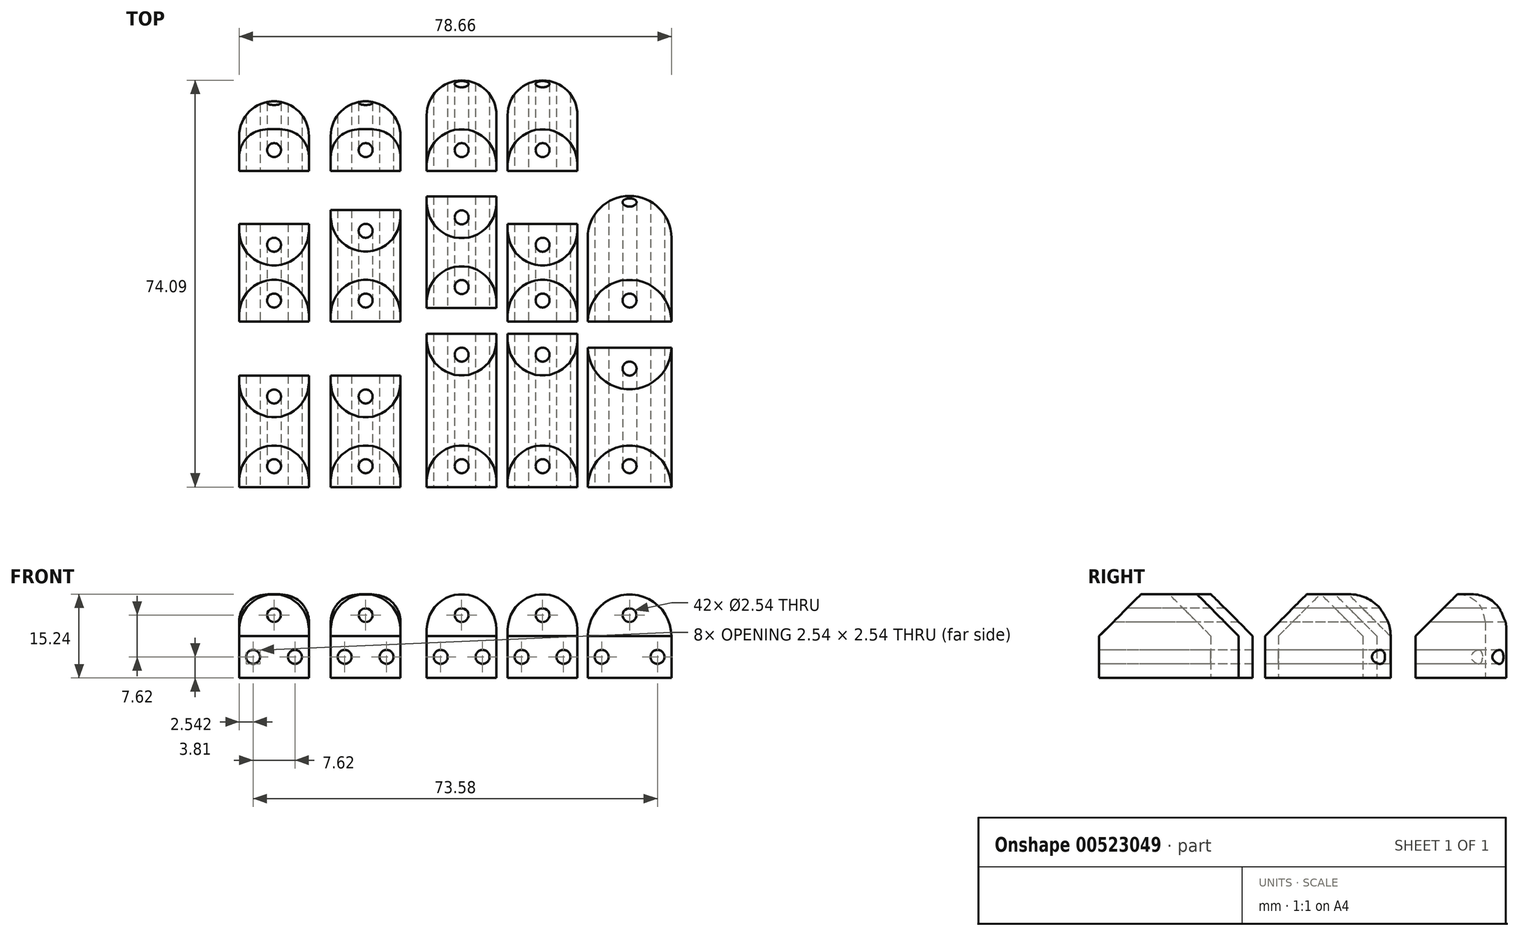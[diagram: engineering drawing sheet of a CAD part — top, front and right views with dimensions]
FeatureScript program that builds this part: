
annotation { "Feature Type Name" : "Feature", "Feature Type Description" : "" }
export const myFeature = defineFeature(function(context is Context, id is Id, definition is map)
    precondition{}
    {
        {
            var Q0;
            Q0=qCreatedBy(makeId("Top.planeOp"),FACE);
            var sketch = newSketch(context, id + "F0", { "sketchPlane" : qUnion([Q0])});
            skLineSegment(sketch, "E0.bottom", {"start": v(-28.43, 45.4) * mm, "end": v(-15.73, 45.4) * mm});
            skLineSegment(sketch, "E0.top", {"start": v(-28.43, 32.7) * mm, "end": v(-15.73, 32.7) * mm});
            skLineSegment(sketch, "E0.left", {"start": v(-28.43, 45.4) * mm, "end": v(-28.43, 32.7) * mm});
            skLineSegment(sketch, "E0.right", {"start": v(-15.73, 45.4) * mm, "end": v(-15.73, 32.7) * mm});
            skLineSegment(sketch, "E1.bottom", {"start": v(-28.43, 23.07) * mm, "end": v(-15.73, 23.07) * mm});
            skLineSegment(sketch, "E1.top", {"start": v(-28.43, 5.3) * mm, "end": v(-15.73, 5.3) * mm});
            skLineSegment(sketch, "E1.left", {"start": v(-28.43, 23.07) * mm, "end": v(-28.43, 5.3) * mm});
            skLineSegment(sketch, "E1.right", {"start": v(-15.73, 23.07) * mm, "end": v(-15.73, 5.3) * mm});
            skLineSegment(sketch, "E2.bottom", {"start": v(-28.43, -4.56) * mm, "end": v(-15.73, -4.56) * mm});
            skLineSegment(sketch, "E2.top", {"start": v(-28.43, -24.88) * mm, "end": v(-15.73, -24.88) * mm});
            skLineSegment(sketch, "E2.left", {"start": v(-28.43, -4.56) * mm, "end": v(-28.43, -24.88) * mm});
            skLineSegment(sketch, "E2.right", {"start": v(-15.73, -4.56) * mm, "end": v(-15.73, -24.88) * mm});
            skLineSegment(sketch, "E3.bottom", {"start": v(-11.76, 45.4) * mm, "end": v(0.94, 45.4) * mm});
            skLineSegment(sketch, "E3.top", {"start": v(-11.76, 32.7) * mm, "end": v(0.94, 32.7) * mm});
            skLineSegment(sketch, "E3.left", {"start": v(-11.76, 45.4) * mm, "end": v(-11.76, 32.7) * mm});
            skLineSegment(sketch, "E3.right", {"start": v(0.94, 45.4) * mm, "end": v(0.94, 32.7) * mm});
            skLineSegment(sketch, "E4.bottom", {"start": v(-11.76, 25.61) * mm, "end": v(0.94, 25.61) * mm});
            skLineSegment(sketch, "E4.top", {"start": v(-11.76, 5.3) * mm, "end": v(0.94, 5.3) * mm});
            skLineSegment(sketch, "E4.left", {"start": v(-11.76, 25.61) * mm, "end": v(-11.76, 5.3) * mm});
            skLineSegment(sketch, "E4.right", {"start": v(0.94, 25.61) * mm, "end": v(0.94, 5.3) * mm});
            skLineSegment(sketch, "E5.bottom", {"start": v(-11.76, -4.56) * mm, "end": v(0.94, -4.56) * mm});
            skLineSegment(sketch, "E5.top", {"start": v(-11.76, -24.88) * mm, "end": v(0.94, -24.88) * mm});
            skLineSegment(sketch, "E5.left", {"start": v(-11.76, -4.56) * mm, "end": v(-11.76, -24.88) * mm});
            skLineSegment(sketch, "E5.right", {"start": v(0.94, -4.56) * mm, "end": v(0.94, -24.88) * mm});
            skLineSegment(sketch, "E6.bottom", {"start": v(5.7, 49.2) * mm, "end": v(18.4, 49.2) * mm});
            skLineSegment(sketch, "E6.top", {"start": v(5.7, 32.7) * mm, "end": v(18.4, 32.7) * mm});
            skLineSegment(sketch, "E6.left", {"start": v(5.7, 49.2) * mm, "end": v(5.7, 32.7) * mm});
            skLineSegment(sketch, "E6.right", {"start": v(18.4, 49.2) * mm, "end": v(18.4, 32.7) * mm});
            skLineSegment(sketch, "E7.bottom", {"start": v(5.7, 28.07) * mm, "end": v(18.4, 28.07) * mm});
            skLineSegment(sketch, "E7.top", {"start": v(5.7, 7.75) * mm, "end": v(18.4, 7.75) * mm});
            skLineSegment(sketch, "E7.left", {"start": v(5.7, 28.07) * mm, "end": v(5.7, 7.75) * mm});
            skLineSegment(sketch, "E7.right", {"start": v(18.4, 28.07) * mm, "end": v(18.4, 7.75) * mm});
            skLineSegment(sketch, "E8.bottom", {"start": v(5.7, 3.06) * mm, "end": v(18.4, 3.06) * mm});
            skLineSegment(sketch, "E8.top", {"start": v(5.7, -24.88) * mm, "end": v(18.4, -24.88) * mm});
            skLineSegment(sketch, "E8.left", {"start": v(5.7, 3.06) * mm, "end": v(5.7, -24.88) * mm});
            skLineSegment(sketch, "E8.right", {"start": v(18.4, 3.06) * mm, "end": v(18.4, -24.88) * mm});
            skLineSegment(sketch, "E9.bottom", {"start": v(20.44, 49.2) * mm, "end": v(33.14, 49.2) * mm});
            skLineSegment(sketch, "E9.top", {"start": v(20.44, 32.7) * mm, "end": v(33.14, 32.7) * mm});
            skLineSegment(sketch, "E9.left", {"start": v(20.44, 49.2) * mm, "end": v(20.44, 32.7) * mm});
            skLineSegment(sketch, "E9.right", {"start": v(33.14, 49.2) * mm, "end": v(33.14, 32.7) * mm});
            skLineSegment(sketch, "E10.bottom", {"start": v(20.44, 23.07) * mm, "end": v(33.14, 23.07) * mm});
            skLineSegment(sketch, "E10.top", {"start": v(20.44, 5.3) * mm, "end": v(33.14, 5.3) * mm});
            skLineSegment(sketch, "E10.left", {"start": v(20.44, 23.07) * mm, "end": v(20.44, 5.3) * mm});
            skLineSegment(sketch, "E10.right", {"start": v(33.14, 23.07) * mm, "end": v(33.14, 5.3) * mm});
            skLineSegment(sketch, "E11.bottom", {"start": v(20.44, 3.06) * mm, "end": v(33.14, 3.06) * mm});
            skLineSegment(sketch, "E11.top", {"start": v(20.44, -24.88) * mm, "end": v(33.14, -24.88) * mm});
            skLineSegment(sketch, "E11.left", {"start": v(20.44, 3.06) * mm, "end": v(20.44, -24.88) * mm});
            skLineSegment(sketch, "E11.right", {"start": v(33.14, 3.06) * mm, "end": v(33.14, -24.88) * mm});
            skLineSegment(sketch, "E12.bottom", {"start": v(35, 28.15) * mm, "end": v(50.23, 28.15) * mm});
            skLineSegment(sketch, "E12.top", {"start": v(35, 5.3) * mm, "end": v(50.23, 5.3) * mm});
            skLineSegment(sketch, "E12.left", {"start": v(35, 28.15) * mm, "end": v(35, 5.3) * mm});
            skLineSegment(sketch, "E12.right", {"start": v(50.23, 28.15) * mm, "end": v(50.23, 5.3) * mm});
            skLineSegment(sketch, "E13.bottom", {"start": v(35, 0.52) * mm, "end": v(50.23, 0.52) * mm});
            skLineSegment(sketch, "E13.top", {"start": v(35, -24.88) * mm, "end": v(50.23, -24.88) * mm});
            skLineSegment(sketch, "E13.left", {"start": v(35, 0.52) * mm, "end": v(35, -24.88) * mm});
            skLineSegment(sketch, "E13.right", {"start": v(50.23, 0.52) * mm, "end": v(50.23, -24.88) * mm});
            skSolve(sketch);
        }
        {
            var Q0;
            Q0=makeQuery(id+"F0.imprint","IMPRINT",FACE,{"disambiguationData":[TD([[makeQuery(id+"F0.imprint","IMPRINT",EDGE,{"derivedFrom":sQuery(id+"F0.wireOp",EDGE,"E0.bottom")}),-1.0]])]});
            var Q1;
            Q1=makeQuery(id+"F0.imprint","IMPRINT",FACE,{"disambiguationData":[TD([[makeQuery(id+"F0.imprint","IMPRINT",EDGE,{"derivedFrom":sQuery(id+"F0.wireOp",EDGE,"E1.bottom")}),-1.0]])]});
            var Q2;
            Q2=makeQuery(id+"F0.imprint","IMPRINT",FACE,{"disambiguationData":[TD([[makeQuery(id+"F0.imprint","IMPRINT",EDGE,{"derivedFrom":sQuery(id+"F0.wireOp",EDGE,"E2.bottom")}),-1.0]])]});
            var Q3;
            Q3=makeQuery(id+"F0.imprint","IMPRINT",FACE,{"disambiguationData":[TD([[makeQuery(id+"F0.imprint","IMPRINT",EDGE,{"derivedFrom":sQuery(id+"F0.wireOp",EDGE,"E5.bottom")}),-1.0]])]});
            var Q4;
            Q4=makeQuery(id+"F0.imprint","IMPRINT",FACE,{"disambiguationData":[TD([[makeQuery(id+"F0.imprint","IMPRINT",EDGE,{"derivedFrom":sQuery(id+"F0.wireOp",EDGE,"E4.bottom")}),-1.0]])]});
            var Q5;
            Q5=makeQuery(id+"F0.imprint","IMPRINT",FACE,{"disambiguationData":[TD([[makeQuery(id+"F0.imprint","IMPRINT",EDGE,{"derivedFrom":sQuery(id+"F0.wireOp",EDGE,"E3.bottom")}),-1.0]])]});
            var Q6;
            Q6=makeQuery(id+"F0.imprint","IMPRINT",FACE,{"disambiguationData":[TD([[makeQuery(id+"F0.imprint","IMPRINT",EDGE,{"derivedFrom":sQuery(id+"F0.wireOp",EDGE,"E6.bottom")}),-1.0]])]});
            var Q7;
            Q7=makeQuery(id+"F0.imprint","IMPRINT",FACE,{"disambiguationData":[TD([[makeQuery(id+"F0.imprint","IMPRINT",EDGE,{"derivedFrom":sQuery(id+"F0.wireOp",EDGE,"E7.bottom")}),-1.0]])]});
            var Q8;
            Q8=makeQuery(id+"F0.imprint","IMPRINT",FACE,{"disambiguationData":[TD([[makeQuery(id+"F0.imprint","IMPRINT",EDGE,{"derivedFrom":sQuery(id+"F0.wireOp",EDGE,"E8.bottom")}),-1.0]])]});
            var Q9;
            Q9=makeQuery(id+"F0.imprint","IMPRINT",FACE,{"disambiguationData":[TD([[makeQuery(id+"F0.imprint","IMPRINT",EDGE,{"derivedFrom":sQuery(id+"F0.wireOp",EDGE,"E11.bottom")}),-1.0]])]});
            var Q10;
            Q10=makeQuery(id+"F0.imprint","IMPRINT",FACE,{"disambiguationData":[TD([[makeQuery(id+"F0.imprint","IMPRINT",EDGE,{"derivedFrom":sQuery(id+"F0.wireOp",EDGE,"E10.bottom")}),-1.0]])]});
            var Q11;
            Q11=makeQuery(id+"F0.imprint","IMPRINT",FACE,{"disambiguationData":[TD([[makeQuery(id+"F0.imprint","IMPRINT",EDGE,{"derivedFrom":sQuery(id+"F0.wireOp",EDGE,"E9.bottom")}),-1.0]])]});
            var Q12;
            Q12=makeQuery(id+"F0.imprint","IMPRINT",FACE,{"disambiguationData":[TD([[makeQuery(id+"F0.imprint","IMPRINT",EDGE,{"derivedFrom":sQuery(id+"F0.wireOp",EDGE,"E12.bottom")}),-1.0]])]});
            var Q13;
            Q13=makeQuery(id+"F0.imprint","IMPRINT",FACE,{"disambiguationData":[TD([[makeQuery(id+"F0.imprint","IMPRINT",EDGE,{"derivedFrom":sQuery(id+"F0.wireOp",EDGE,"E13.bottom")}),-1.0]])]});
            extrude(context, id + "F1", {"entities" : qUnion([Q0, Q1, Q2, Q3, Q4, Q5, Q6, Q7, Q8, Q9, Q10, Q11, Q12, Q13]), "depth" : 15.24 * mm, "offsetDistance" : 25.4 * mm});
        }
        {
            var Q0;
            Q0=makeQuery(id+"F1.opExtrude","CAP_EDGE",EDGE,{"disambiguationData":[OSD([sQuery(id+"F0.wireOp",EDGE,"E0.top")])],"isStart":false});
            var Q1;
            Q1=makeQuery(id+"F1.opExtrude","CAP_EDGE",EDGE,{"disambiguationData":[OSD([sQuery(id+"F0.wireOp",EDGE,"E1.bottom")])],"isStart":false});
            var Q2;
            Q2=makeQuery(id+"F1.opExtrude","CAP_EDGE",EDGE,{"disambiguationData":[OSD([sQuery(id+"F0.wireOp",EDGE,"E1.top")])],"isStart":false});
            var Q3;
            Q3=makeQuery(id+"F1.opExtrude","CAP_EDGE",EDGE,{"disambiguationData":[OSD([sQuery(id+"F0.wireOp",EDGE,"E2.bottom")])],"isStart":false});
            var Q4;
            Q4=makeQuery(id+"F1.opExtrude","CAP_EDGE",EDGE,{"disambiguationData":[OSD([sQuery(id+"F0.wireOp",EDGE,"E2.top")])],"isStart":false});
            chamfer(context, id + "F2", {"entities" : qUnion([Q0, Q1, Q2, Q3, Q4]), "width" : 7.62 * mm, "tangentPropagation" : true});
        }
        {
            var Q0;
            Q0=makeQuery(id+"F1.opExtrude","SWEPT_EDGE",EDGE,{"disambiguationData":[OSD([sQuery(id+"F0.wireOp",EDGE,"E0.bottom"),sQuery(id+"F0.wireOp",EDGE,"E0.right")])]});
            var Q1;
            Q1=makeQuery(id+"F1.opExtrude","SWEPT_EDGE",EDGE,{"disambiguationData":[OSD([sQuery(id+"F0.wireOp",EDGE,"E0.bottom"),sQuery(id+"F0.wireOp",EDGE,"E0.left")])]});
            var Q2;
            Q2=makeQuery(id+"F1.opExtrude","SWEPT_EDGE",EDGE,{"disambiguationData":[OSD([sQuery(id+"F0.wireOp",EDGE,"E3.bottom"),sQuery(id+"F0.wireOp",EDGE,"E3.left")])]});
            var Q3;
            Q3=makeQuery(id+"F1.opExtrude","SWEPT_EDGE",EDGE,{"disambiguationData":[OSD([sQuery(id+"F0.wireOp",EDGE,"E3.bottom"),sQuery(id+"F0.wireOp",EDGE,"E3.right")])]});
            var Q4;
            Q4=makeQuery(id+"F1.opExtrude","SWEPT_EDGE",EDGE,{"disambiguationData":[OSD([sQuery(id+"F0.wireOp",EDGE,"E6.bottom"),sQuery(id+"F0.wireOp",EDGE,"E6.right")])]});
            var Q5;
            Q5=makeQuery(id+"F1.opExtrude","SWEPT_EDGE",EDGE,{"disambiguationData":[OSD([sQuery(id+"F0.wireOp",EDGE,"E9.bottom"),sQuery(id+"F0.wireOp",EDGE,"E9.right")])]});
            var Q6;
            Q6=makeQuery(id+"F1.opExtrude","SWEPT_EDGE",EDGE,{"disambiguationData":[OSD([sQuery(id+"F0.wireOp",EDGE,"E9.bottom"),sQuery(id+"F0.wireOp",EDGE,"E9.left")])]});
            var Q7;
            Q7=makeQuery(id+"F1.opExtrude","SWEPT_EDGE",EDGE,{"disambiguationData":[OSD([sQuery(id+"F0.wireOp",EDGE,"E6.bottom"),sQuery(id+"F0.wireOp",EDGE,"E6.left")])]});
            fillet(context, id + "F3", {"entities" : qUnion([Q0, Q1, Q2, Q3, Q4, Q5, Q6, Q7]), "radius" : 6.35 * mm, "tangentPropagation" : true, "allowEdgeOverflow" : false});
        }
        {
            var Q0;
            Q0=makeQuery(id+"F1.opExtrude","CAP_EDGE",EDGE,{"disambiguationData":[OSD([sQuery(id+"F0.wireOp",EDGE,"E1.left")])],"isStart":false});
            var Q1;
            Q1=makeQuery(id+"F1.opExtrude","CAP_EDGE",EDGE,{"disambiguationData":[OSD([sQuery(id+"F0.wireOp",EDGE,"E1.right")])],"isStart":false});
            var Q2;
            Q2=makeQuery(id+"F1.opExtrude","CAP_EDGE",EDGE,{"disambiguationData":[OSD([sQuery(id+"F0.wireOp",EDGE,"E2.left")])],"isStart":false});
            var Q3;
            Q3=makeQuery(id+"F1.opExtrude","CAP_EDGE",EDGE,{"disambiguationData":[OSD([sQuery(id+"F0.wireOp",EDGE,"E2.right")])],"isStart":false});
            fillet(context, id + "F4", {"entities" : qUnion([Q0, Q1, Q2, Q3]), "radius" : 6.35 * mm, "tangentPropagation" : true, "allowEdgeOverflow" : false});
        }
        {
            var Q0;
            Q0=makeQuery(id+"F1.opExtrude","CAP_EDGE",EDGE,{"disambiguationData":[OSD([sQuery(id+"F0.wireOp",EDGE,"E3.top")])],"isStart":false});
            var Q1;
            Q1=makeQuery(id+"F1.opExtrude","CAP_EDGE",EDGE,{"disambiguationData":[OSD([sQuery(id+"F0.wireOp",EDGE,"E4.bottom")])],"isStart":false});
            var Q2;
            Q2=makeQuery(id+"F1.opExtrude","CAP_EDGE",EDGE,{"disambiguationData":[OSD([sQuery(id+"F0.wireOp",EDGE,"E4.top")])],"isStart":false});
            var Q3;
            Q3=makeQuery(id+"F1.opExtrude","CAP_EDGE",EDGE,{"disambiguationData":[OSD([sQuery(id+"F0.wireOp",EDGE,"E5.bottom")])],"isStart":false});
            var Q4;
            Q4=makeQuery(id+"F1.opExtrude","CAP_EDGE",EDGE,{"disambiguationData":[OSD([sQuery(id+"F0.wireOp",EDGE,"E5.top")])],"isStart":false});
            var Q5;
            Q5=makeQuery(id+"F1.opExtrude","CAP_EDGE",EDGE,{"disambiguationData":[OSD([sQuery(id+"F0.wireOp",EDGE,"E6.top")])],"isStart":false});
            var Q6;
            Q6=makeQuery(id+"F1.opExtrude","CAP_EDGE",EDGE,{"disambiguationData":[OSD([sQuery(id+"F0.wireOp",EDGE,"E7.bottom")])],"isStart":false});
            var Q7;
            Q7=makeQuery(id+"F1.opExtrude","CAP_EDGE",EDGE,{"disambiguationData":[OSD([sQuery(id+"F0.wireOp",EDGE,"E7.top")])],"isStart":false});
            var Q8;
            Q8=makeQuery(id+"F1.opExtrude","CAP_EDGE",EDGE,{"disambiguationData":[OSD([sQuery(id+"F0.wireOp",EDGE,"E8.bottom")])],"isStart":false});
            var Q9;
            Q9=makeQuery(id+"F1.opExtrude","CAP_EDGE",EDGE,{"disambiguationData":[OSD([sQuery(id+"F0.wireOp",EDGE,"E8.top")])],"isStart":false});
            var Q10;
            Q10=makeQuery(id+"F1.opExtrude","CAP_EDGE",EDGE,{"disambiguationData":[OSD([sQuery(id+"F0.wireOp",EDGE,"E9.bottom")])],"isStart":false});
            var Q11;
            Q11=makeQuery(id+"F1.opExtrude","CAP_EDGE",EDGE,{"disambiguationData":[OSD([sQuery(id+"F0.wireOp",EDGE,"E9.top")])],"isStart":false});
            var Q12;
            Q12=makeQuery(id+"F1.opExtrude","CAP_EDGE",EDGE,{"disambiguationData":[OSD([sQuery(id+"F0.wireOp",EDGE,"E10.bottom")])],"isStart":false});
            var Q13;
            Q13=makeQuery(id+"F1.opExtrude","CAP_EDGE",EDGE,{"disambiguationData":[OSD([sQuery(id+"F0.wireOp",EDGE,"E10.top")])],"isStart":false});
            var Q14;
            Q14=makeQuery(id+"F1.opExtrude","CAP_EDGE",EDGE,{"disambiguationData":[OSD([sQuery(id+"F0.wireOp",EDGE,"E11.bottom")])],"isStart":false});
            var Q15;
            Q15=makeQuery(id+"F1.opExtrude","CAP_EDGE",EDGE,{"disambiguationData":[OSD([sQuery(id+"F0.wireOp",EDGE,"E11.top")])],"isStart":false});
            var Q16;
            Q16=makeQuery(id+"F1.opExtrude","CAP_EDGE",EDGE,{"disambiguationData":[OSD([sQuery(id+"F0.wireOp",EDGE,"E12.top")])],"isStart":false});
            var Q17;
            Q17=makeQuery(id+"F1.opExtrude","CAP_EDGE",EDGE,{"disambiguationData":[OSD([sQuery(id+"F0.wireOp",EDGE,"E13.bottom")])],"isStart":false});
            var Q18;
            Q18=makeQuery(id+"F1.opExtrude","CAP_EDGE",EDGE,{"disambiguationData":[OSD([sQuery(id+"F0.wireOp",EDGE,"E13.top")])],"isStart":false});
            chamfer(context, id + "F5", {"entities" : qUnion([Q0, Q1, Q2, Q3, Q4, Q5, Q6, Q7, Q8, Q9, Q10, Q11, Q12, Q13, Q14, Q15, Q16, Q17, Q18]), "width" : 7.62 * mm, "tangentPropagation" : true});
        }
        {
            var Q0;
            Q0=makeQuery(id+"F1.opExtrude","SWEPT_EDGE",EDGE,{"disambiguationData":[OSD([sQuery(id+"F0.wireOp",EDGE,"E12.bottom"),sQuery(id+"F0.wireOp",EDGE,"E12.right")])]});
            var Q1;
            Q1=makeQuery(id+"F1.opExtrude","SWEPT_EDGE",EDGE,{"disambiguationData":[OSD([sQuery(id+"F0.wireOp",EDGE,"E12.bottom"),sQuery(id+"F0.wireOp",EDGE,"E12.left")])]});
            fillet(context, id + "F6", {"entities" : qUnion([Q0, Q1]), "radius" : 7.62 * mm, "tangentPropagation" : true, "allowEdgeOverflow" : false});
        }
        {
            var Q0;
            {var subQ0=sQuery(id+"F0.wireOp",EDGE,"E12.left");var subQ1=sQuery(id+"F0.wireOp",EDGE,"E12.bottom");Q0=makeQuery(id+"F6.opFillet","BLEND_EDGE",EDGE,{"blendedFrom":[makeQuery(id+"F1.opExtrude","SWEPT_EDGE",EDGE,{"disambiguationData":[OSD([subQ1,subQ0])]}),makeQuery(id+"F1.opExtrude","CAP_FACE",FACE,{"disambiguationData":[OSD([subQ1,sQuery(id+"F0.wireOp",EDGE,"E12.top"),subQ0,sQuery(id+"F0.wireOp",EDGE,"E12.right")])],"isStart":false})],"blendedInto":[makeQuery(id+"F1.opExtrude","CAP_FACE",FACE,{"disambiguationData":[OSD([subQ1,sQuery(id+"F0.wireOp",EDGE,"E12.top"),subQ0,sQuery(id+"F0.wireOp",EDGE,"E12.right")])],"isStart":false})]});}
            fillet(context, id + "F7", {"entities" : qUnion([Q0]), "radius" : 7.62 * mm, "tangentPropagation" : true, "allowEdgeOverflow" : false});
        }
        {
            var Q0;
            {var subQ0=sQuery(id+"F0.wireOp",EDGE,"E3.left");var subQ1=sQuery(id+"F0.wireOp",EDGE,"E3.bottom");Q0=makeQuery(id+"F3.opFillet","BLEND_EDGE",EDGE,{"blendedFrom":[makeQuery(id+"F1.opExtrude","SWEPT_EDGE",EDGE,{"disambiguationData":[OSD([subQ1,subQ0])]}),makeQuery(id+"F1.opExtrude","CAP_FACE",FACE,{"disambiguationData":[OSD([subQ1,sQuery(id+"F0.wireOp",EDGE,"E3.top"),subQ0,sQuery(id+"F0.wireOp",EDGE,"E3.right")])],"isStart":false})],"blendedInto":[makeQuery(id+"F1.opExtrude","CAP_FACE",FACE,{"disambiguationData":[OSD([subQ1,sQuery(id+"F0.wireOp",EDGE,"E3.top"),subQ0,sQuery(id+"F0.wireOp",EDGE,"E3.right")])],"isStart":false})]});}
            var Q1;
            {var subQ0=sQuery(id+"F0.wireOp",EDGE,"E0.left");var subQ1=sQuery(id+"F0.wireOp",EDGE,"E0.bottom");Q1=makeQuery(id+"F3.opFillet","BLEND_EDGE",EDGE,{"blendedFrom":[makeQuery(id+"F1.opExtrude","SWEPT_EDGE",EDGE,{"disambiguationData":[OSD([subQ1,subQ0])]}),makeQuery(id+"F1.opExtrude","CAP_FACE",FACE,{"disambiguationData":[OSD([subQ1,sQuery(id+"F0.wireOp",EDGE,"E0.top"),subQ0,sQuery(id+"F0.wireOp",EDGE,"E0.right")])],"isStart":false})],"blendedInto":[makeQuery(id+"F1.opExtrude","CAP_FACE",FACE,{"disambiguationData":[OSD([subQ1,sQuery(id+"F0.wireOp",EDGE,"E0.top"),subQ0,sQuery(id+"F0.wireOp",EDGE,"E0.right")])],"isStart":false})]});}
            fillet(context, id + "F8", {"entities" : qUnion([Q0, Q1]), "radius" : 5.08 * mm, "tangentPropagation" : true, "allowEdgeOverflow" : false});
        }
        {
            var Q0;
            Q0=makeQuery(id+"F1.opExtrude","CAP_EDGE",EDGE,{"disambiguationData":[OSD([sQuery(id+"F0.wireOp",EDGE,"E4.left")])],"isStart":false});
            var Q1;
            Q1=makeQuery(id+"F1.opExtrude","CAP_EDGE",EDGE,{"disambiguationData":[OSD([sQuery(id+"F0.wireOp",EDGE,"E4.right")])],"isStart":false});
            var Q2;
            Q2=makeQuery(id+"F1.opExtrude","CAP_EDGE",EDGE,{"disambiguationData":[OSD([sQuery(id+"F0.wireOp",EDGE,"E5.right")])],"isStart":false});
            var Q3;
            Q3=makeQuery(id+"F1.opExtrude","CAP_EDGE",EDGE,{"disambiguationData":[OSD([sQuery(id+"F0.wireOp",EDGE,"E5.left")])],"isStart":false});
            var Q4;
            Q4=makeQuery(id+"F1.opExtrude","CAP_EDGE",EDGE,{"disambiguationData":[OSD([sQuery(id+"F0.wireOp",EDGE,"E7.right")])],"isStart":false});
            var Q5;
            Q5=makeQuery(id+"F1.opExtrude","CAP_EDGE",EDGE,{"disambiguationData":[OSD([sQuery(id+"F0.wireOp",EDGE,"E7.left")])],"isStart":false});
            var Q6;
            Q6=makeQuery(id+"F1.opExtrude","CAP_EDGE",EDGE,{"disambiguationData":[OSD([sQuery(id+"F0.wireOp",EDGE,"E8.right")])],"isStart":false});
            var Q7;
            Q7=makeQuery(id+"F1.opExtrude","CAP_EDGE",EDGE,{"disambiguationData":[OSD([sQuery(id+"F0.wireOp",EDGE,"E8.left")])],"isStart":false});
            var Q8;
            Q8=makeQuery(id+"F1.opExtrude","CAP_EDGE",EDGE,{"disambiguationData":[OSD([sQuery(id+"F0.wireOp",EDGE,"E10.right")])],"isStart":false});
            var Q9;
            Q9=makeQuery(id+"F1.opExtrude","CAP_EDGE",EDGE,{"disambiguationData":[OSD([sQuery(id+"F0.wireOp",EDGE,"E10.left")])],"isStart":false});
            var Q10;
            Q10=makeQuery(id+"F1.opExtrude","CAP_EDGE",EDGE,{"disambiguationData":[OSD([sQuery(id+"F0.wireOp",EDGE,"E11.right")])],"isStart":false});
            var Q11;
            Q11=makeQuery(id+"F1.opExtrude","CAP_EDGE",EDGE,{"disambiguationData":[OSD([sQuery(id+"F0.wireOp",EDGE,"E11.left")])],"isStart":false});
            fillet(context, id + "F9", {"entities" : qUnion([Q0, Q1, Q2, Q3, Q4, Q5, Q6, Q7, Q8, Q9, Q10, Q11]), "radius" : 6.35 * mm, "tangentPropagation" : true, "allowEdgeOverflow" : false});
        }
        {
            var Q0;
            Q0=makeQuery(id+"F1.opExtrude","CAP_EDGE",EDGE,{"disambiguationData":[OSD([sQuery(id+"F0.wireOp",EDGE,"E13.left")])],"isStart":false});
            var Q1;
            Q1=makeQuery(id+"F1.opExtrude","CAP_EDGE",EDGE,{"disambiguationData":[OSD([sQuery(id+"F0.wireOp",EDGE,"E13.right")])],"isStart":false});
            fillet(context, id + "F10", {"entities" : qUnion([Q0, Q1]), "radius" : 7.62 * mm, "tangentPropagation" : true, "allowEdgeOverflow" : false});
        }
        {
            var Q0;
            {var subQ0=sQuery(id+"F0.wireOp",EDGE,"E6.left");var subQ1=sQuery(id+"F0.wireOp",EDGE,"E6.bottom");Q0=makeQuery(id+"F3.opFillet","BLEND_EDGE",EDGE,{"blendedFrom":[makeQuery(id+"F1.opExtrude","SWEPT_EDGE",EDGE,{"disambiguationData":[OSD([subQ1,subQ0])]}),makeQuery(id+"F1.opExtrude","CAP_FACE",FACE,{"disambiguationData":[OSD([subQ1,sQuery(id+"F0.wireOp",EDGE,"E6.top"),subQ0,sQuery(id+"F0.wireOp",EDGE,"E6.right")])],"isStart":false})],"blendedInto":[makeQuery(id+"F1.opExtrude","CAP_FACE",FACE,{"disambiguationData":[OSD([subQ1,sQuery(id+"F0.wireOp",EDGE,"E6.top"),subQ0,sQuery(id+"F0.wireOp",EDGE,"E6.right")])],"isStart":false})]});}
            var Q1;
            {var subQ0=sQuery(id+"F0.wireOp",EDGE,"E9.left");var subQ1=sQuery(id+"F0.wireOp",EDGE,"E9.bottom");Q1=makeQuery(id+"F3.opFillet","BLEND_EDGE",EDGE,{"blendedFrom":[makeQuery(id+"F1.opExtrude","SWEPT_EDGE",EDGE,{"disambiguationData":[OSD([subQ1,subQ0])]}),makeQuery(id+"F1.opExtrude","CAP_FACE",FACE,{"disambiguationData":[OSD([subQ1,sQuery(id+"F0.wireOp",EDGE,"E9.top"),subQ0,sQuery(id+"F0.wireOp",EDGE,"E9.right")])],"isStart":false})],"blendedInto":[makeQuery(id+"F1.opExtrude","CAP_FACE",FACE,{"disambiguationData":[OSD([subQ1,sQuery(id+"F0.wireOp",EDGE,"E9.top"),subQ0,sQuery(id+"F0.wireOp",EDGE,"E9.right")])],"isStart":false})]});}
            fillet(context, id + "F11", {"entities" : qUnion([Q0, Q1]), "radius" : 6.35 * mm, "tangentPropagation" : true, "allowEdgeOverflow" : false});
        }
        {
            var Q0;
            Q0=makeQuery(id+"F1.opExtrude","SWEPT_FACE",FACE,{"disambiguationData":[OSD([sQuery(id+"F0.wireOp",EDGE,"E2.top")])]});
            var sketch = newSketch(context, id + "F12", { "sketchPlane" : qUnion([Q0])});
            skCircle(sketch, "E14", {"center": v(-25.89, 3.81) * mm, "radius": 1.27 * mm});
            skCircle(sketch, "E15", {"center": v(-18.27, 3.81) * mm, "radius": 1.27 * mm});
            skCircle(sketch, "E16", {"center": v(-22.08, 11.43) * mm, "radius": 1.27 * mm});
            skPoint(sketch, "E16.centerSnap0", {"position": v(-22.08, 7.62) * mm});
            skCircle(sketch, "E17", {"center": v(-9.22, 3.81) * mm, "radius": 1.27 * mm});
            skCircle(sketch, "E18", {"center": v(-1.6, 3.81) * mm, "radius": 1.27 * mm});
            skLineSegment(sketch, "E19.0", {"start": v(0.94, 7.62) * mm, "end": v(-11.76, 7.62) * mm});
            skLineSegment(sketch, "E20.0", {"start": v(18.4, 7.62) * mm, "end": v(5.7, 7.62) * mm});
            skLineSegment(sketch, "E21.0", {"start": v(33.14, 7.62) * mm, "end": v(20.44, 7.62) * mm});
            skLineSegment(sketch, "E22.0", {"start": v(50.23, 7.62) * mm, "end": v(35, 7.62) * mm});
            skLineSegment(sketch, "E23.0", {"start": v(-11.76, 7.62) * mm, "end": v(-11.76, 0) * mm});
            skLineSegment(sketch, "E24.0", {"start": v(0.94, 7.62) * mm, "end": v(0.94, 0) * mm});
            skLineSegment(sketch, "E25.0", {"start": v(5.7, 7.62) * mm, "end": v(5.7, 0) * mm});
            skLineSegment(sketch, "E26.0", {"start": v(18.4, 7.62) * mm, "end": v(18.4, 0) * mm});
            skLineSegment(sketch, "E27.0", {"start": v(20.44, 7.62) * mm, "end": v(20.44, 0) * mm});
            skPoint(sketch, "E28.0", {"position": v(33.14, 3.81) * mm});
            skLineSegment(sketch, "E29.0", {"start": v(33.14, 7.62) * mm, "end": v(33.14, 0) * mm});
            skLineSegment(sketch, "E30.0", {"start": v(35, 7.62) * mm, "end": v(35, 0) * mm});
            skLineSegment(sketch, "E31.0", {"start": v(50.23, 7.62) * mm, "end": v(50.23, 0) * mm});
            skPoint(sketch, "E32.0", {"position": v(50.23, 3.8) * mm});
            skCircle(sketch, "E33", {"center": v(-5.41, 11.43) * mm, "radius": 1.27 * mm});
            skPoint(sketch, "E33.centerSnap0", {"position": v(-5.41, 7.62) * mm});
            skCircle(sketch, "E34", {"center": v(8.25, 3.81) * mm, "radius": 1.27 * mm});
            skCircle(sketch, "E35", {"center": v(15.87, 3.81) * mm, "radius": 1.27 * mm});
            skCircle(sketch, "E36", {"center": v(12.06, 11.43) * mm, "radius": 1.27 * mm});
            skPoint(sketch, "E36.centerSnap0", {"position": v(12.06, 7.62) * mm});
            skCircle(sketch, "E37", {"center": v(26.79, 11.43) * mm, "radius": 1.27 * mm});
            skPoint(sketch, "E37.centerSnap0", {"position": v(26.79, 7.62) * mm});
            skCircle(sketch, "E38", {"center": v(22.98, 3.81) * mm, "radius": 1.27 * mm});
            skCircle(sketch, "E39", {"center": v(30.6, 3.81) * mm, "radius": 1.27 * mm});
            skCircle(sketch, "E40", {"center": v(37.53, 3.81) * mm, "radius": 1.27 * mm});
            skCircle(sketch, "E41", {"center": v(47.7, 3.81) * mm, "radius": 1.27 * mm});
            skCircle(sketch, "E42", {"center": v(42.61, 11.43) * mm, "radius": 1.27 * mm});
            skPoint(sketch, "E42.centerSnap0", {"position": v(42.61, 7.62) * mm});
            skSolve(sketch);
        }
        {
            var Q0;
            Q0=makeQuery(id+"F12.imprint","IMPRINT",FACE,{"disambiguationData":[TD([[makeQuery(id+"F12.imprint","IMPRINT",EDGE,{"derivedFrom":sQuery(id+"F12.wireOp",EDGE,"E16")}),1.0]])]});
            var Q1;
            Q1=makeQuery(id+"F12.imprint","IMPRINT",FACE,{"disambiguationData":[TD([[makeQuery(id+"F12.imprint","IMPRINT",EDGE,{"derivedFrom":sQuery(id+"F12.wireOp",EDGE,"E14")}),1.0]])]});
            var Q2;
            Q2=makeQuery(id+"F12.imprint","IMPRINT",FACE,{"disambiguationData":[TD([[makeQuery(id+"F12.imprint","IMPRINT",EDGE,{"derivedFrom":sQuery(id+"F12.wireOp",EDGE,"E15")}),1.0]])]});
            var Q3;
            Q3=makeQuery(id+"F12.imprint","IMPRINT",FACE,{"disambiguationData":[TD([[makeQuery(id+"F12.imprint","IMPRINT",EDGE,{"derivedFrom":sQuery(id+"F12.wireOp",EDGE,"E33")}),1.0]])]});
            var Q4;
            Q4=makeQuery(id+"F12.imprint","IMPRINT",FACE,{"disambiguationData":[TD([[makeQuery(id+"F12.imprint","IMPRINT",EDGE,{"derivedFrom":sQuery(id+"F12.wireOp",EDGE,"E17")}),1.0]])]});
            var Q5;
            Q5=makeQuery(id+"F12.imprint","IMPRINT",FACE,{"disambiguationData":[TD([[makeQuery(id+"F12.imprint","IMPRINT",EDGE,{"derivedFrom":sQuery(id+"F12.wireOp",EDGE,"E18")}),1.0]])]});
            var Q6;
            Q6=makeQuery(id+"F12.imprint","IMPRINT",FACE,{"disambiguationData":[TD([[makeQuery(id+"F12.imprint","IMPRINT",EDGE,{"derivedFrom":sQuery(id+"F12.wireOp",EDGE,"E36")}),1.0]])]});
            var Q7;
            Q7=makeQuery(id+"F12.imprint","IMPRINT",FACE,{"disambiguationData":[TD([[makeQuery(id+"F12.imprint","IMPRINT",EDGE,{"derivedFrom":sQuery(id+"F12.wireOp",EDGE,"E34")}),1.0]])]});
            var Q8;
            Q8=makeQuery(id+"F12.imprint","IMPRINT",FACE,{"disambiguationData":[TD([[makeQuery(id+"F12.imprint","IMPRINT",EDGE,{"derivedFrom":sQuery(id+"F12.wireOp",EDGE,"E35")}),1.0]])]});
            var Q9;
            Q9=makeQuery(id+"F12.imprint","IMPRINT",FACE,{"disambiguationData":[TD([[makeQuery(id+"F12.imprint","IMPRINT",EDGE,{"derivedFrom":sQuery(id+"F12.wireOp",EDGE,"E37")}),1.0]])]});
            var Q10;
            Q10=makeQuery(id+"F12.imprint","IMPRINT",FACE,{"disambiguationData":[TD([[makeQuery(id+"F12.imprint","IMPRINT",EDGE,{"derivedFrom":sQuery(id+"F12.wireOp",EDGE,"E38")}),1.0]])]});
            var Q11;
            Q11=makeQuery(id+"F12.imprint","IMPRINT",FACE,{"disambiguationData":[TD([[makeQuery(id+"F12.imprint","IMPRINT",EDGE,{"derivedFrom":sQuery(id+"F12.wireOp",EDGE,"E39")}),1.0]])]});
            var Q12;
            Q12=makeQuery(id+"F12.imprint","IMPRINT",FACE,{"disambiguationData":[TD([[makeQuery(id+"F12.imprint","IMPRINT",EDGE,{"derivedFrom":sQuery(id+"F12.wireOp",EDGE,"E42")}),1.0]])]});
            var Q13;
            Q13=makeQuery(id+"F12.imprint","IMPRINT",FACE,{"disambiguationData":[TD([[makeQuery(id+"F12.imprint","IMPRINT",EDGE,{"derivedFrom":sQuery(id+"F12.wireOp",EDGE,"E40")}),1.0]])]});
            var Q14;
            Q14=makeQuery(id+"F12.imprint","IMPRINT",FACE,{"disambiguationData":[TD([[makeQuery(id+"F12.imprint","IMPRINT",EDGE,{"derivedFrom":sQuery(id+"F12.wireOp",EDGE,"E41")}),1.0]])]});
            extrude(context, id + "F13", {"entities" : qUnion([Q0, Q1, Q2, Q3, Q4, Q5, Q6, Q7, Q8, Q9, Q10, Q11, Q12, Q13, Q14]), "operationType" : NewBodyOperationType.REMOVE, "endBound" : BoundingType.THROUGH_ALL, "oppositeDirection" : true, "depth" : 25.4 * mm, "offsetDistance" : 25.4 * mm});
        }
    });
